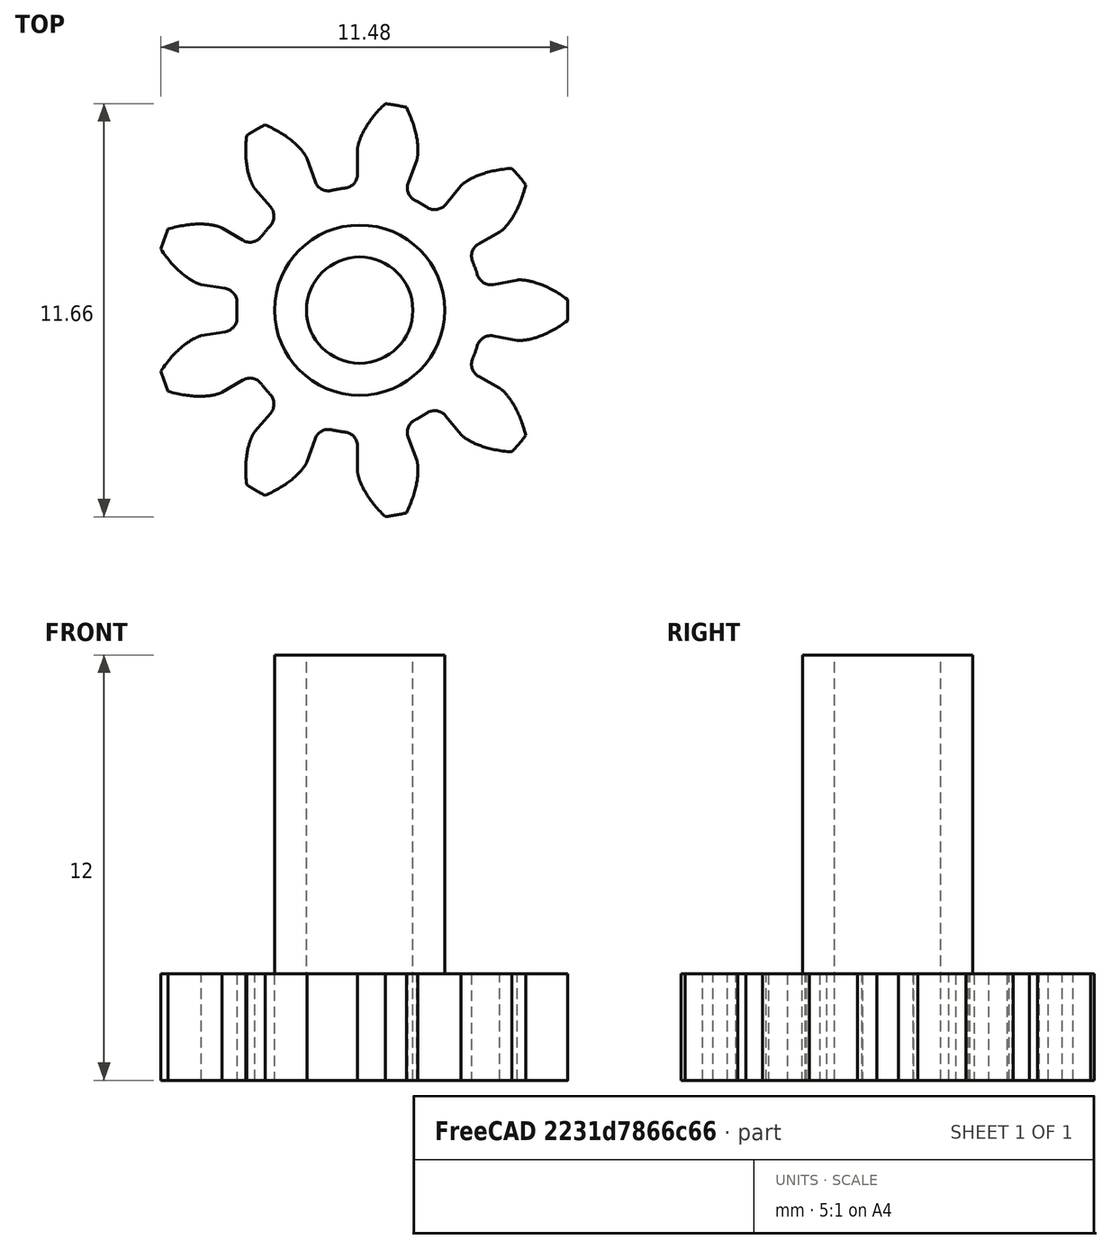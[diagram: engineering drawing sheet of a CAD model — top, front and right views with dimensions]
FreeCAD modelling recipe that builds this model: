
FCSTD DOCUMENT  (FreeCAD 0.17R13541 (Git))
Label: gear 9 exterior shaft (new)
License: All rights reserved
LicenseURL: http://en.wikipedia.org/wiki/All_rights_reserved
objects: Part::Cylinder×3, Part::Cut×2, Part::Part2DObjectPython×1, Part::Extrusion×1, Part::MultiFuse×1
note: 8 computed .brp shape members not serialized (recipe doc carries the construction recipe); baked Part::Feature solids carry a one-line shape summary decoded from their .brp

FEATURE [Part::Part2DObjectPython] InvoluteGear  label="Engranaje 3 raw"  # Draft 2D object (typed FeaturePython)
  ExternalGear = true
  HighPrecision = true
  Modules = 1.067
  NumberOfTeeth = 9
  PressureAngle = 20
  expr: Modules = 1.0669999999999999
FEATURE [Part::Extrusion] Extrude  label="Engranaje 3 extruido"
  Base = -> InvoluteGear
  Dir = (0,0,1)
  DirMode = 2
  FaceMakerClass = Part::FaceMakerBullseye
  LengthFwd = 3
  LengthRev = 0
  Solid = true
  Symmetric = false
FEATURE [Part::Cylinder] Cylinder  label="Cilindro"
  Angle = 360
  AttacherType = Attacher::AttachEngine3D
  Height = 10
  Radius = 1.5
FEATURE [Part::Cut] Cut  label="Engranaje 3 agujereado"
  Base = -> Extrude
  Refine = true
  Tool = -> Cylinder
FEATURE [Part::Cylinder] Cylinder001  label="Cilindro exterior"
  Angle = 360
  AttacherType = Attacher::AttachEngine3D
  Height = 9
  Placement = pos=(0,0,3) rot=(0,0,1;0rad)
  Radius = 2.4
FEATURE [Part::Cylinder] Cylinder002  label="Cilindro interior"
  Angle = 360
  AttacherType = Attacher::AttachEngine3D
  Height = 21
  Placement = pos=(0,0,-2) rot=(0,0,1;0rad)
  Radius = 1.5
FEATURE [Part::MultiFuse] Fusion
  Refine = true
  Shapes = -> [Cut,Cylinder001]
FEATURE [Part::Cut] Cut001  label="Engranaje 3 final"
  Base = -> Fusion
  Refine = true
  Tool = -> Cylinder002
